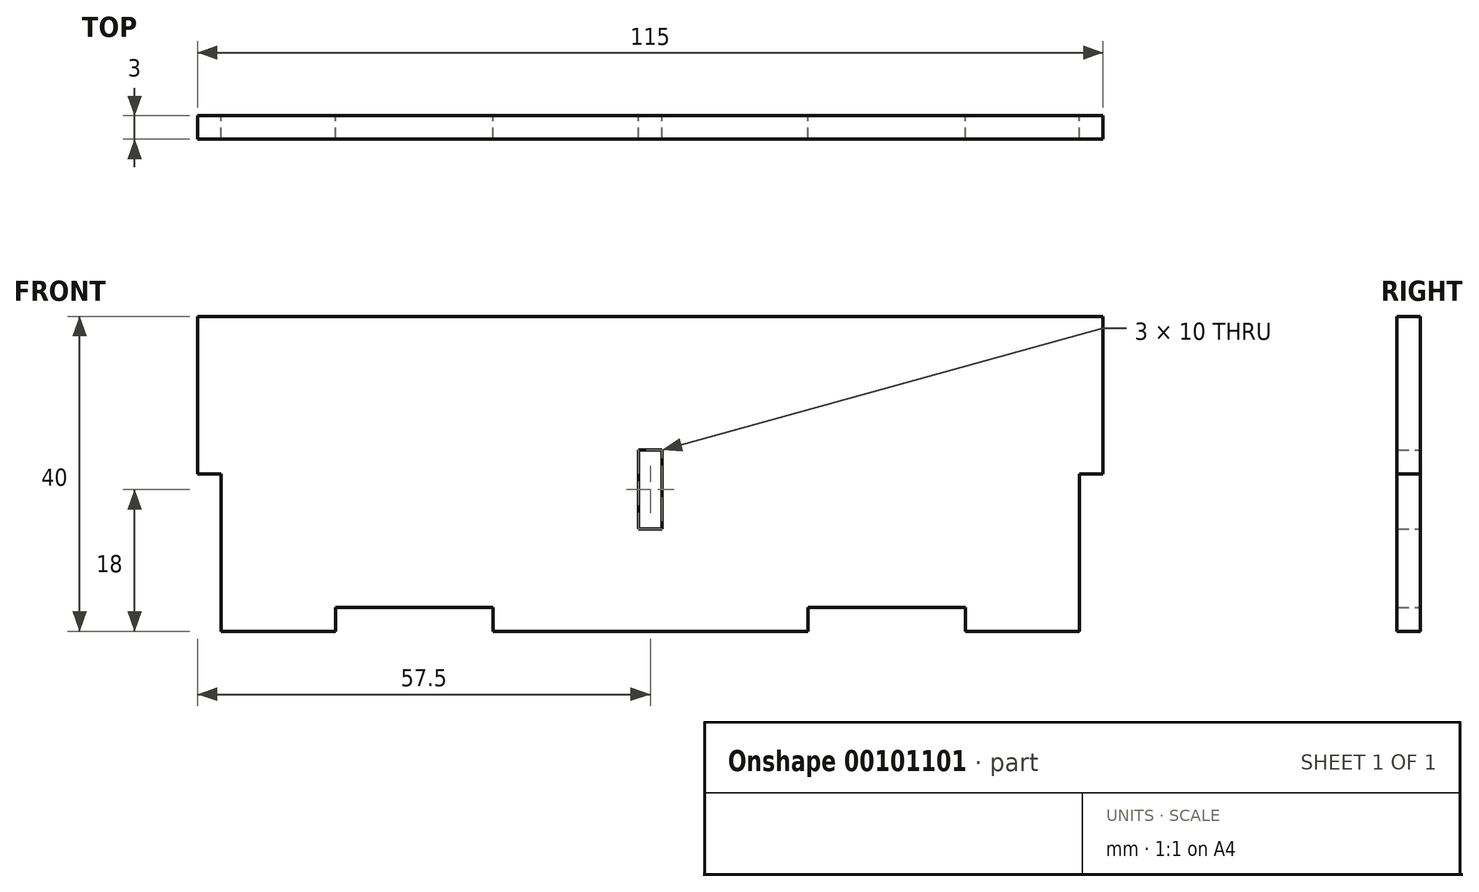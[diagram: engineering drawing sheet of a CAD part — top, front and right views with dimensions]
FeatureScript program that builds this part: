
annotation { "Feature Type Name" : "Feature", "Feature Type Description" : "" }
export const myFeature = defineFeature(function(context is Context, id is Id, definition is map)
    precondition{}
    {
        {
            var Q0;
            Q0=qCreatedBy(makeId("Front.planeOp"),FACE);
            var sketch = newSketch(context, id + "F0", { "sketchPlane" : qUnion([Q0])});
            skLineSegment(sketch, "E0.bottom", {"start": v(54.5, -20) * mm, "end": v(40, -20) * mm});
            skLineSegment(sketch, "E0.top", {"start": v(57.5, 20) * mm, "end": v(-57.5, 20) * mm});
            skLineSegment(sketch, "E0.left", {"start": v(57.5, 0) * mm, "end": v(57.5, 20) * mm});
            skLineSegment(sketch, "E0.right", {"start": v(-57.5, 0) * mm, "end": v(-57.5, 20) * mm});
            skLineSegment(sketch, "E1.top", {"start": v(20, -17) * mm, "end": v(40, -17) * mm});
            skLineSegment(sketch, "E1.left", {"start": v(20, -20) * mm, "end": v(20, -17) * mm});
            skLineSegment(sketch, "E1.right", {"start": v(40, -20) * mm, "end": v(40, -17) * mm});
            skLineSegment(sketch, "E2.bottom", {"start": v(57.5, 0) * mm, "end": v(54.5, 0) * mm});
            skLineSegment(sketch, "E2.right", {"start": v(54.5, 0) * mm, "end": v(54.5, -20) * mm});
            skLineSegment(sketch, "E3.trimOffspring", {"start": v(20, -20) * mm, "end": v(-20, -20) * mm});
            skLineSegment(sketch, "E4.MirrorCS", {"start": v(-57.5, 0) * mm, "end": v(-54.5, 0) * mm});
            skLineSegment(sketch, "E5.MirrorCS", {"start": v(-40, -20) * mm, "end": v(-40, -17) * mm});
            skLineSegment(sketch, "E6.MirrorCS", {"start": v(-20, -20) * mm, "end": v(-20, -17) * mm});
            skLineSegment(sketch, "E7.MirrorCS", {"start": v(-54.5, 0) * mm, "end": v(-54.5, -20) * mm});
            skLineSegment(sketch, "E8.MirrorCS", {"start": v(-54.5, -20) * mm, "end": v(-40, -20) * mm});
            skLineSegment(sketch, "E9.MirrorCS", {"start": v(-20, -17) * mm, "end": v(-40, -17) * mm});
            skLineSegment(sketch, "E10.trimOffspring", {"start": v(-40, -20) * mm, "end": v(-54.5, -20) * mm});
            skLineSegment(sketch, "E11", {"start": v(0, 3) * mm, "end": v(1.5, 3) * mm});
            skLineSegment(sketch, "E12", {"start": v(1.5, 3) * mm, "end": v(1.5, -7) * mm});
            skLineSegment(sketch, "E13", {"start": v(1.5, -7) * mm, "end": v(0, -7) * mm});
            skLineSegment(sketch, "E14.MirrorCS", {"start": v(-1.5, -7) * mm, "end": v(0, -7) * mm});
            skLineSegment(sketch, "E15.MirrorCS", {"start": v(0, 3) * mm, "end": v(-1.5, 3) * mm});
            skLineSegment(sketch, "E16.MirrorCS", {"start": v(-1.5, 3) * mm, "end": v(-1.5, -7) * mm});
            skSolve(sketch);
        }
        {
            var Q0;
            Q0 = qSketchRegion(id + "F0", true);
            extrude(context, id + "F1", {"entities" : qUnion([Q0]), "depth" : 3 * mm});
        }
    });
